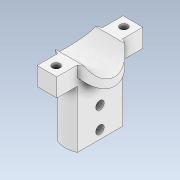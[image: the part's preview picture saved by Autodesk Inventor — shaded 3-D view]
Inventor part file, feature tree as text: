
AUTODESK INVENTOR PART (.ipt)
format: ipt  version: 2022 (Build 260153000, 153)  size: 357,376 bytes
history: native  units: mm
features: extrude x25, sketch x25, projected_geometry x12, plane x2
ambient origin geometry x8: Origin, YZ Plane, XZ Plane, XY Plane, X Axis, Y Axis, Z Axis, Center Point
bodies: Solid1 (feature_tree)
feature tree (64):
  extrude  "Extrusion1"  Depth=22.0mm
  extrude  "Extrusion2"  Depth=10.0mm
  extrude  "Extrusion3"  Depth=3.0mm
  extrude  "Extrusion4"  Depth=10.0mm TaperAngle=0.0deg
  extrude  "Extrusion5"  Depth=3.0mm
  extrude  "Extrusion6"  Depth=10.0mm
  plane  "Work Plane1"
  extrude  "Extrusion7"  Depth=29.0mm
  extrude  "Extrusion8"  TaperAngle=0.0deg  [1 undecoded]
  extrude  "Extrusion9"  Depth=10.0mm TaperAngle=0.0deg
  plane  "Work Plane2"
  extrude  "Extrusion12"  Depth=10.0mm TaperAngle=0.0deg
  extrude  "Extrusion13"  TaperAngle=0.0deg  [1 undecoded]
  extrude  "Extrusion16"  Depth=25.0mm TaperAngle=0.0deg
  extrude  "Extrusion17"  Depth=10.0mm
  extrude  "Extrusion18"  Depth=7.0mm
  extrude  "Extrusion19"  TaperAngle=0.0deg  [1 undecoded]
  extrude  "Extrusion20"  TaperAngle=0.0deg  [1 undecoded]
  extrude  "Extrusion21"  Depth=12.671mm
  extrude  "Extrusion22"  Depth=6.0mm
  extrude  "Extrusion23"  Depth=10.0mm TaperAngle=0.0deg
  sketch  "Sketch26"  dims[d66=10.0mm d67=0.0mm d68=0.0mm d69=0.0mm]
  extrude  "Extrusion24"  TaperAngle=0.0deg  [1 undecoded]
  extrude  "Extrusion25"  TaperAngle=0.0deg  [1 undecoded]
  extrude  "Extrusion26"  Depth=4.329mm TaperAngle=0.0deg
  extrude  "Extrusion27"  [1 undecoded]
  extrude  "Extrusion28"  [1 undecoded]
  extrude  "Extrusion29"  [1 undecoded]
  sketch  "Sketch1"  dims[d0=28.0mm d1=22.0mm]
  sketch  "Sketch2"  dims[d2=10.0mm d3=0.0mm d4=35.0mm]
  sketch  "Sketch3"  dims[d5=3.0mm d6=0.0mm d7=15.0mm]
  sketch  "Sketch4"  dims[d8=3.0mm d9=0.0mm d10=10.0mm d11=0.0mm]
  projected_geometry  "Projected Loop1"
  projected_geometry  "Projected Loop2"
  sketch  "Sketch5"  dims[d12=3.0mm d13=5.0mm]
  sketch  "Sketch6"  dims[d14=2.0mm d15=10.0mm]
  sketch  "Sketch7"  dims[d16=0.0mm d17=0.0mm d18=29.0mm]
  sketch  "Sketch8"  dims[d19=10.0mm d20=0.0mm d21=0.0mm d22=0.0mm]
  sketch  "Sketch9"  dims[d23=10.0mm d24=0.0mm d25=13.0mm d26=0.0mm]
  projected_geometry  "Projected Loop3"
  sketch  "Sketch12"  dims[d31=10.0mm d32=0.0mm d33=13.0mm d34=0.0mm]
  projected_geometry  "Projected Loop5"
  sketch  "Sketch13"  dims[d39=2.8mm d40=0.0mm d41=0.0mm d42=0.0mm]
  projected_geometry  "Projected Loop6"
  sketch  "Sketch17"  dims[d43=25.0mm d44=0.0mm d45=25.0mm d46=0.0mm]
  sketch  "Sketch18"  dims[d47=10.0mm d48=0.0mm d49=7.0mm]
  projected_geometry  "Projected Loop9"
  projected_geometry  "Projected Loop10"
  sketch  "Sketch20"  dims[d50=7.0mm d51=7.0mm]
  projected_geometry  "Projected Loop12"
  sketch  "Sketch21"  dims[d52=7.0mm d53=0.0mm d54=0.0mm]
  sketch  "Sketch22"  dims[d55=40.0mm d56=0.0mm d57=0.0mm]
  sketch  "Sketch23"  dims[d58=0.0mm d59=0.0mm d60=12.671mm]
  sketch  "Sketch24"  dims[d61=15.0mm d62=6.0mm]
  sketch  "Sketch25"  dims[d63=6.0mm d64=10.0mm d65=0.0mm]
  sketch  "Sketch27"  dims[d70=40.0mm d71=0.0mm d72=0.0mm]
  projected_geometry  "Projected Loop13"
  projected_geometry  "Projected Loop14"
  sketch  "Sketch28"  dims[d73=0.0mm d74=0.0mm d75=4.329mm d76=0.0mm]
  projected_geometry  "Projected Loop15"
  sketch  "Sketch29"
  sketch  "Sketch30"
  sketch  "Sketch31"
  projected_geometry  "Projected Loop16"
note: 9 required parameter values undecoded (feature->parameter linkage not recoverable at this tier; creation-order binding heuristic only, values carry confidence <= 0.55)
